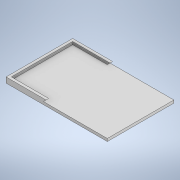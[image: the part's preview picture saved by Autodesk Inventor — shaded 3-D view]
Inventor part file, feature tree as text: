
AUTODESK INVENTOR PART (.ipt)
format: ipt  version: 2022.2 (Build 262287010, 287A)  size: 127,488 bytes
history: native  units: in
note: dims shown in document units (in); Inventor stores cm internally (conversion verified against a paired STEP export)
features: extrude x3, sketch x3, other x1, mirror x1
ambient origin geometry x8: Origin, YZ Plane, XZ Plane, XY Plane, X Axis, Y Axis, Z Axis, Center Point
bodies: Body1 (feature_tree), Body2 (feature_tree), Body3 (feature_tree), Body4 (feature_tree), Body5 (feature_tree)
feature tree (8):
  other  "Sólido1"
  extrude  "Extrusión1"  Depth=1.9685in
  extrude  "Extrusión4"  Depth=0.0787in
  extrude  "Extrusión5"  Depth=0.0787in TaperAngle=0.0deg
  mirror  "Simetría2"
  sketch  "Boceto1"  dims[d0=2.9921in d1=1.9685in]
  sketch  "Boceto2"  dims[d2=0.0787in d3=0.0in d14=0.0787in]
  sketch  "Boceto5"  dims[d15=0.0787in d16=0.0in d19=0.0787in d20=0.0in d4=0.0197in d5=0.0344in d6=0.0197in d7=0.0344in]
